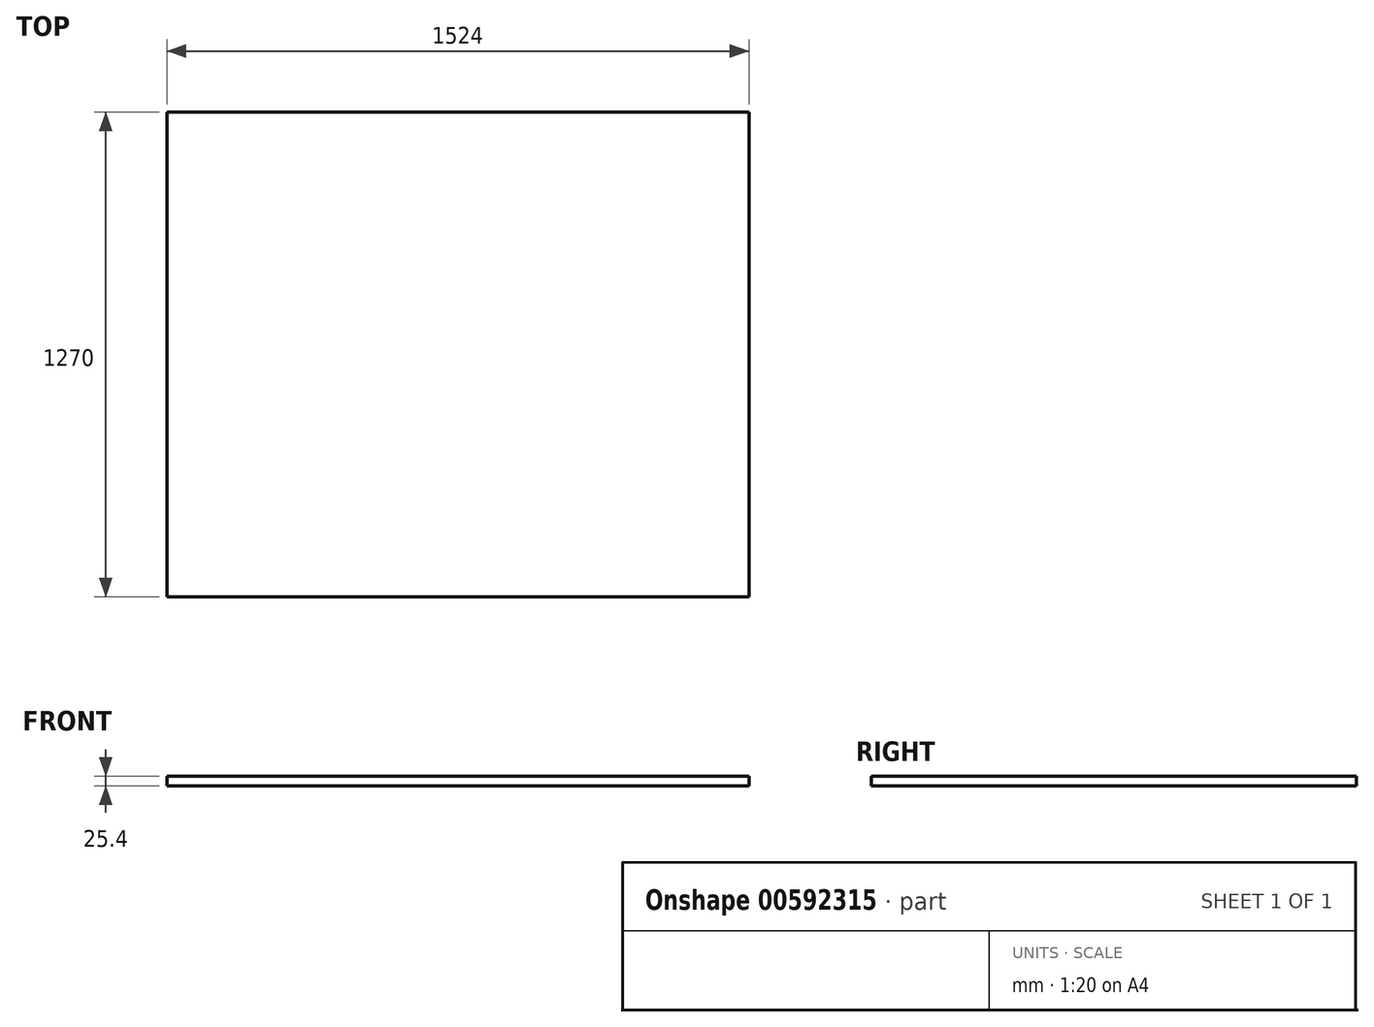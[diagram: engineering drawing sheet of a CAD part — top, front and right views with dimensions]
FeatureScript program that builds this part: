
annotation { "Feature Type Name" : "Feature", "Feature Type Description" : "" }
export const myFeature = defineFeature(function(context is Context, id is Id, definition is map)
    precondition{}
    {
        {
            var Q0;
            Q0=qCreatedBy(makeId("Top.planeOp"),FACE);
            var sketch = newSketch(context, id + "F0", { "sketchPlane" : qUnion([Q0])});
            skLineSegment(sketch, "E0.bottom", {"start": v(0, 0) * mm, "end": v(1524, 0) * mm});
            skLineSegment(sketch, "E0.top", {"start": v(0, -1270) * mm, "end": v(1524, -1270) * mm});
            skLineSegment(sketch, "E0.left", {"start": v(0, 0) * mm, "end": v(0, -1270) * mm});
            skLineSegment(sketch, "E0.right", {"start": v(1524, 0) * mm, "end": v(1524, -1270) * mm});
            skSolve(sketch);
        }
        {
            var Q0;
            Q0=makeQuery(id+"F0.imprint","IMPRINT",FACE,{"disambiguationData":[TD([[makeQuery(id+"F0.imprint","IMPRINT",EDGE,{"derivedFrom":sQuery(id+"F0.wireOp",EDGE,"E0.bottom")}),-1.0]])]});
            extrude(context, id + "F1", {"entities" : qUnion([Q0]), "depth" : 25.4 * mm, "offsetDistance" : 25.4 * mm});
        }
    });
